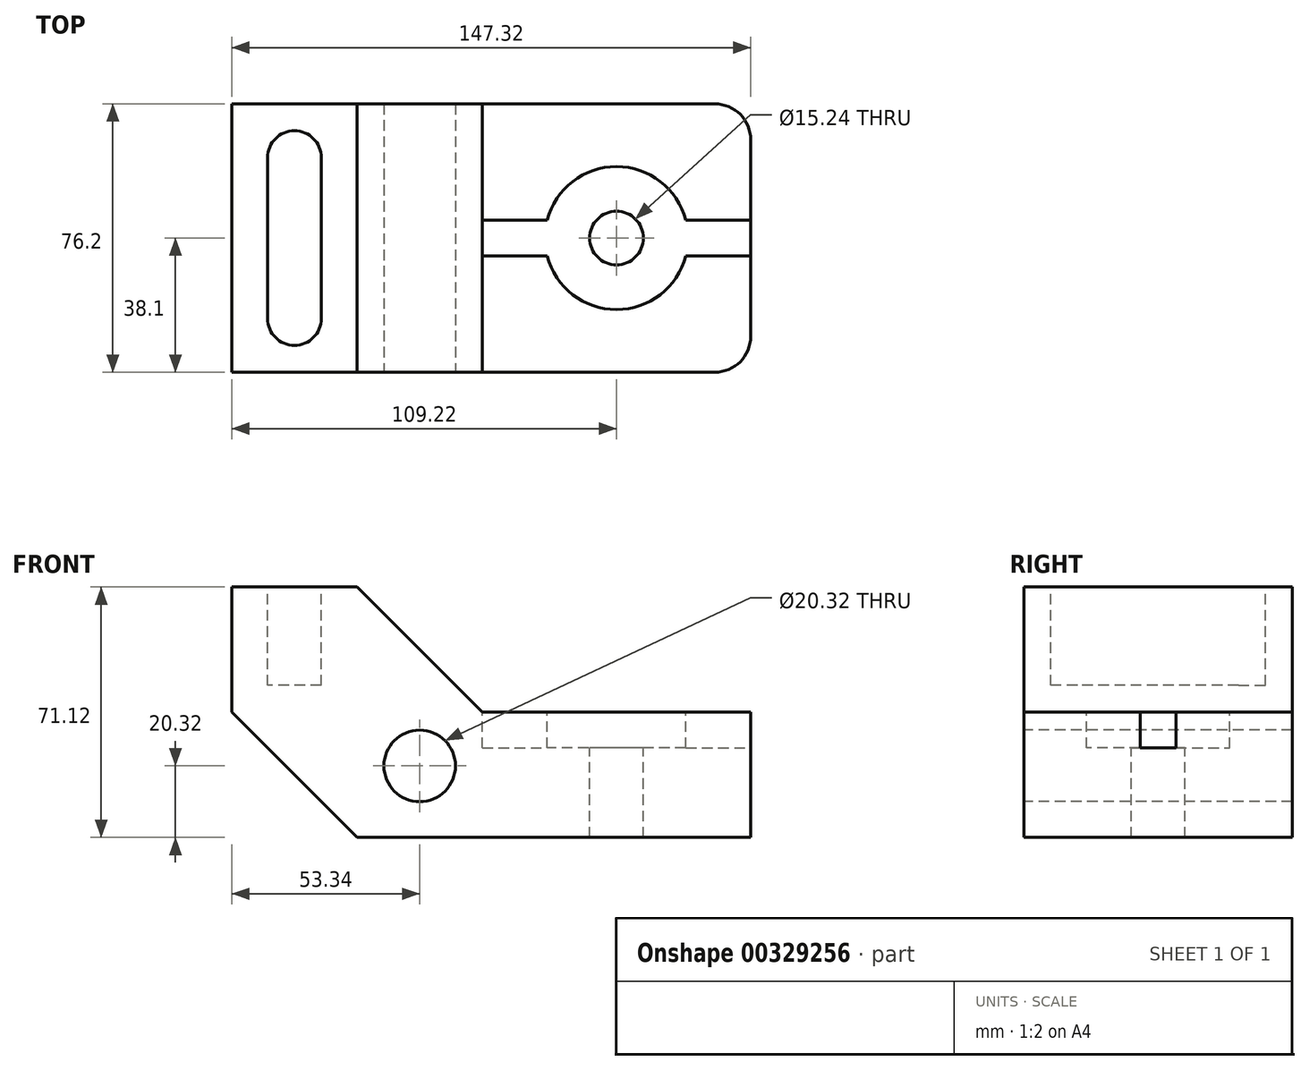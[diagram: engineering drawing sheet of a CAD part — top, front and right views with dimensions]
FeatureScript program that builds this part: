
annotation { "Feature Type Name" : "Feature", "Feature Type Description" : "" }
export const myFeature = defineFeature(function(context is Context, id is Id, definition is map)
    precondition{}
    {
        {
            var Q0;
            Q0=qCreatedBy(makeId("Front.planeOp"),FACE);
            var sketch = newSketch(context, id + "F0", { "sketchPlane" : qUnion([Q0])});
            skLineSegment(sketch, "E0", {"start": v(0, 0) * mm, "end": v(0, 71.12) * mm});
            skLineSegment(sketch, "E1", {"start": v(0, 71.12) * mm, "end": v(35.56, 71.12) * mm});
            skLineSegment(sketch, "E2", {"start": v(0, 0) * mm, "end": v(147.32, 0) * mm});
            skLineSegment(sketch, "E3", {"start": v(147.32, 0) * mm, "end": v(147.32, 35.56) * mm});
            skLineSegment(sketch, "E4", {"start": v(147.32, 35.56) * mm, "end": v(71.12, 35.56) * mm});
            skLineSegment(sketch, "E5", {"start": v(35.56, 71.12) * mm, "end": v(71.12, 35.56) * mm});
            skSolve(sketch);
        }
        {
            var Q0;
            Q0=makeQuery(id+"F0.imprint","IMPRINT",FACE,{"disambiguationData":[TD([[makeQuery(id+"F0.imprint","IMPRINT",EDGE,{"derivedFrom":sQuery(id+"F0.wireOp",EDGE,"E0")}),-1.0]])]});
            extrude(context, id + "F1", {"entities" : qUnion([Q0]), "endBound" : BoundingType.SYMMETRIC, "depth" : 76.2 * mm});
        }
        {
            var Q0;
            Q0=makeQuery(id+"F1.opExtrude","CAP_FACE",FACE,{"disambiguationData":[OSD([sQuery(id+"F0.wireOp",EDGE,"E0"),sQuery(id+"F0.wireOp",EDGE,"E1"),sQuery(id+"F0.wireOp",EDGE,"E2"),sQuery(id+"F0.wireOp",EDGE,"E3"),sQuery(id+"F0.wireOp",EDGE,"E4"),sQuery(id+"F0.wireOp",EDGE,"E5")])],"isStart":false});
            var sketch = newSketch(context, id + "F2", { "sketchPlane" : qUnion([Q0])});
            skLineSegment(sketch, "E6", {"start": v(0, 0) * mm, "end": v(35.56, 0) * mm});
            skLineSegment(sketch, "E7", {"start": v(0, 0) * mm, "end": v(0, 35.56) * mm});
            skLineSegment(sketch, "E8", {"start": v(0, 35.56) * mm, "end": v(35.56, 0) * mm});
            skSolve(sketch);
        }
        {
            var Q0;
            Q0=makeQuery(id+"F2.imprint","IMPRINT",FACE,{"disambiguationData":[TD([[makeQuery(id+"F2.imprint","IMPRINT",EDGE,{"derivedFrom":sQuery(id+"F2.wireOp",EDGE,"E6")}),1.0]])]});
            extrude(context, id + "F3", {"entities" : qUnion([Q0]), "operationType" : NewBodyOperationType.REMOVE, "endBound" : BoundingType.THROUGH_ALL, "oppositeDirection" : true, "depth" : 25.4 * mm});
        }
        {
            var Q0;
            Q0=makeQuery(id+"F1.opExtrude","CAP_EDGE",EDGE,{"disambiguationData":[OSD([sQuery(id+"F0.wireOp",EDGE,"E3")])],"isStart":false});
            var Q1;
            Q1=makeQuery(id+"F1.opExtrude","CAP_EDGE",EDGE,{"disambiguationData":[OSD([sQuery(id+"F0.wireOp",EDGE,"E3")])],"isStart":true});
            fillet(context, id + "F4", {"entities" : qUnion([Q0, Q1]), "radius" : 10.16 * mm, "tangentPropagation" : true, "allowEdgeOverflow" : false});
        }
        {
            var Q0;
            Q0=makeQuery(id+"F1.opExtrude","SWEPT_FACE",FACE,{"disambiguationData":[OSD([sQuery(id+"F0.wireOp",EDGE,"E1")])]});
            var sketch = newSketch(context, id + "F5", { "sketchPlane" : qUnion([Q0])});
            skLineSegment(sketch, "E9", {"start": v(10.16, 22.86) * mm, "end": v(10.16, -22.86) * mm});
            skLineSegment(sketch, "E10", {"start": v(25.4, 22.86) * mm, "end": v(25.4, -22.86) * mm});
            skArc(sketch, "E11", {"start": v(25.4, 22.86) * mm, "mid": v(17.78, 30.48) * mm, "end": v(10.16, 22.86) * mm});
            skArc(sketch, "E12", {"start": v(10.16, -22.86) * mm, "mid": v(17.78, -30.48) * mm, "end": v(25.4, -22.86) * mm});
            skSolve(sketch);
        }
        {
            var Q0;
            Q0=makeQuery(id+"F5.imprint","IMPRINT",FACE,{"disambiguationData":[TD([[makeQuery(id+"F5.imprint","IMPRINT",EDGE,{"derivedFrom":sQuery(id+"F5.wireOp",EDGE,"E9")}),1.0]])]});
            extrude(context, id + "F6", {"entities" : qUnion([Q0]), "operationType" : NewBodyOperationType.REMOVE, "oppositeDirection" : true, "depth" : 27.94 * mm});
        }
        {
            var Q0;
            Q0=makeQuery(id+"F1.opExtrude","SWEPT_FACE",FACE,{"disambiguationData":[OSD([sQuery(id+"F0.wireOp",EDGE,"E4")])]});
            var sketch = newSketch(context, id + "F7", { "sketchPlane" : qUnion([Q0])});
            skPoint(sketch, "E13", {"position": v(109.22, 0) * mm});
            skSolve(sketch);
        }
        {
            var Q0;
            Q0=sQuery(id+"F7.wireOp",VERTEX,"E13");
            var Q1;
            Q1=makeQuery(id+"F1.opExtrude","SWEPT_BODY",BODY,{"disambiguationData":[OSD([sQuery(id+"F0.wireOp",EDGE,"E0"),sQuery(id+"F0.wireOp",EDGE,"E1"),sQuery(id+"F0.wireOp",EDGE,"E2"),sQuery(id+"F0.wireOp",EDGE,"E3"),sQuery(id+"F0.wireOp",EDGE,"E4"),sQuery(id+"F0.wireOp",EDGE,"E5")])]});
            hole(context, id + "F8", {"style" : HoleStyle.C_BORE, "endStyle" : HoleEndStyle.THROUGH, "holeDiameter" : 15.24 * mm, "cBoreDiameter" : 40.64 * mm, "cBoreDepth" : 10.16 * mm, "tappedDepth" : 12.7 * mm, "tapClearance" : 3, "locations" : qUnion([Q0]), "scope" : qUnion([Q1])});
        }
        {
            var Q0;
            Q0=makeQuery(id+"F1.opExtrude","SWEPT_FACE",FACE,{"disambiguationData":[OSD([sQuery(id+"F0.wireOp",EDGE,"E4")])]});
            var sketch = newSketch(context, id + "F9", { "sketchPlane" : qUnion([Q0])});
            skLineSegment(sketch, "E14", {"start": v(65.6, 0) * mm, "end": v(151.66, 0) * mm, "construction": true});
            skPoint(sketch, "E14.startSnap0", {"position": v(71.12, 0) * mm});
            skLineSegment(sketch, "E15", {"start": v(71.12, 0) * mm, "end": v(71.12, 5.08) * mm});
            skLineSegment(sketch, "E16", {"start": v(71.12, 5.08) * mm, "end": v(147.32, 5.08) * mm});
            skLineSegment(sketch, "E17", {"start": v(147.32, 5.08) * mm, "end": v(147.32, 0) * mm});
            skLineSegment(sketch, "E18.MirrorCS", {"start": v(71.12, -5.08) * mm, "end": v(147.32, -5.08) * mm});
            skLineSegment(sketch, "E19.MirrorCS", {"start": v(71.12, 0) * mm, "end": v(71.12, -5.08) * mm});
            skLineSegment(sketch, "E20.MirrorCS", {"start": v(147.32, -5.08) * mm, "end": v(147.32, 0) * mm});
            skSolve(sketch);
        }
        {
            var Q0;
            {var subQ7=sQuery(id+"F9.wireOp",EDGE,"E17");Q0=makeQuery(id+"F9.imprint","IMPRINT",FACE,{"disambiguationData":[TD([[makeQuery(id+"F9.imprint","IMPRINT",EDGE,{"derivedFrom":subQ7}),1.0]])]});}
            var Q1;
            {var subQ6=sQuery(id+"F9.wireOp",EDGE,"E15");Q1=makeQuery(id+"F9.imprint","IMPRINT",FACE,{"disambiguationData":[TD([[makeQuery(id+"F9.imprint","IMPRINT",EDGE,{"derivedFrom":subQ6}),-1.0]])]});}
            extrude(context, id + "F10", {"entities" : qUnion([Q0, Q1]), "operationType" : NewBodyOperationType.REMOVE, "oppositeDirection" : true, "depth" : 10.16 * mm});
        }
        {
            var Q0;
            Q0=makeQuery(id+"F1.opExtrude","CAP_FACE",FACE,{"disambiguationData":[OSD([sQuery(id+"F0.wireOp",EDGE,"E0"),sQuery(id+"F0.wireOp",EDGE,"E1"),sQuery(id+"F0.wireOp",EDGE,"E2"),sQuery(id+"F0.wireOp",EDGE,"E3"),sQuery(id+"F0.wireOp",EDGE,"E4"),sQuery(id+"F0.wireOp",EDGE,"E5")])],"isStart":false});
            var sketch = newSketch(context, id + "F11", { "sketchPlane" : qUnion([Q0])});
            skCircle(sketch, "E21", {"center": v(53.34, 20.32) * mm, "radius": 10.16 * mm});
            skSolve(sketch);
        }
        {
            var Q0;
            Q0=makeQuery(id+"F11.imprint","IMPRINT",FACE,{"disambiguationData":[TD([[makeQuery(id+"F11.imprint","IMPRINT",EDGE,{"derivedFrom":sQuery(id+"F11.wireOp",EDGE,"E21")}),1.0]])]});
            extrude(context, id + "F12", {"entities" : qUnion([Q0]), "operationType" : NewBodyOperationType.REMOVE, "endBound" : BoundingType.THROUGH_ALL, "oppositeDirection" : true, "depth" : 25.4 * mm});
        }
    });
